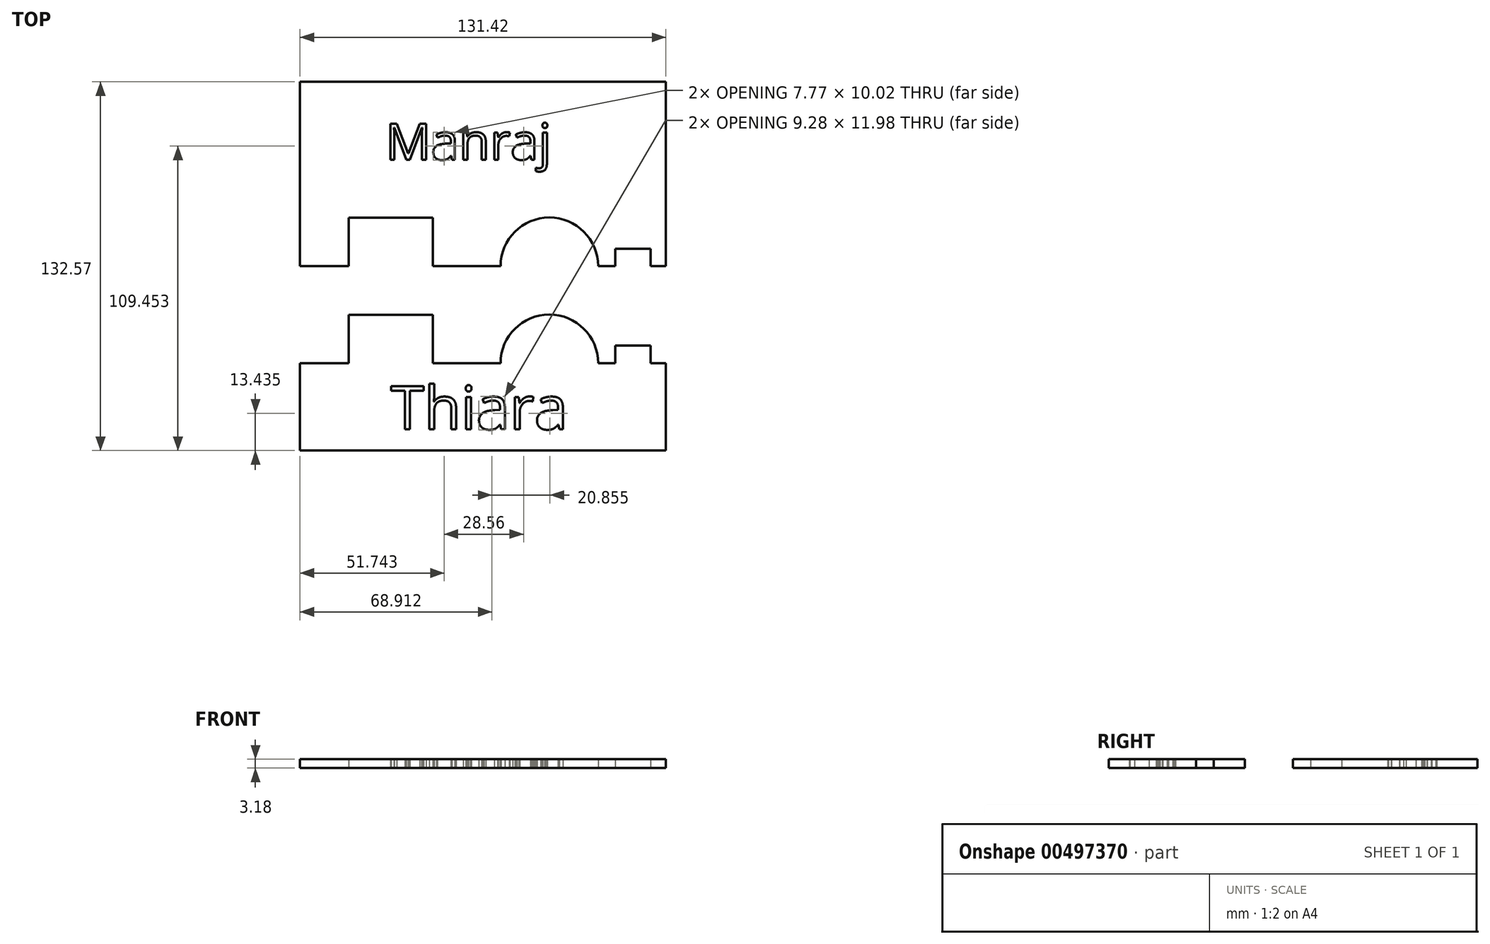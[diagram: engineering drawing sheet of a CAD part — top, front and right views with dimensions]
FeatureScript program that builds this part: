
annotation { "Feature Type Name" : "Feature", "Feature Type Description" : "" }
export const myFeature = defineFeature(function(context is Context, id is Id, definition is map)
    precondition{}
    {
        {
            var Q0;
            Q0=qCreatedBy(makeId("Top.planeOp"),FACE);
            var sketch = newSketch(context, id + "F0", { "sketchPlane" : qUnion([Q0])});
            skLineSegment(sketch, "E0.bottom", {"start": v(-79.32, 79.1) * mm, "end": v(52.1, 79.1) * mm});
            skLineSegment(sketch, "E0.top", {"start": v(-79.32, -53.48) * mm, "end": v(52.1, -53.48) * mm});
            skLineSegment(sketch, "E0.left", {"start": v(-79.32, 79.1) * mm, "end": v(-79.32, 12.8) * mm});
            skLineSegment(sketch, "E0.right", {"start": v(52.1, 79.1) * mm, "end": v(52.1, 12.8) * mm});
            skLineSegment(sketch, "E1", {"start": v(-79.32, 12.8) * mm, "end": v(-61.87, 12.8) * mm});
            skLineSegment(sketch, "E2.top", {"start": v(-61.87, 30.25) * mm, "end": v(-31.63, 30.25) * mm});
            skLineSegment(sketch, "E2.left", {"start": v(-61.87, 12.8) * mm, "end": v(-61.87, 30.25) * mm});
            skLineSegment(sketch, "E2.right", {"start": v(-31.63, 12.8) * mm, "end": v(-31.63, 30.25) * mm});
            skLineSegment(sketch, "E3.trimOffspring", {"start": v(-31.63, 12.8) * mm, "end": v(-7.29, 12.8) * mm});
            skLineSegment(sketch, "E4.trimOffspring", {"start": v(-79.32, -22.1) * mm, "end": v(-79.32, -53.48) * mm});
            skLineSegment(sketch, "E5.top", {"start": v(-79.32, -22.1) * mm, "end": v(-61.87, -22.1) * mm});
            skLineSegment(sketch, "E5.left", {"start": v(-79.32, -53.48) * mm, "end": v(-79.32, -22.1) * mm});
            skLineSegment(sketch, "E5.right", {"start": v(52.1, -53.48) * mm, "end": v(52.1, -22.1) * mm});
            skLineSegment(sketch, "E6.trimOffspring", {"start": v(52.1, -22.1) * mm, "end": v(52.1, -53.48) * mm});
            skLineSegment(sketch, "E7", {"start": v(-61.87, -4.65) * mm, "end": v(-61.87, -22.1) * mm});
            skLineSegment(sketch, "E8", {"start": v(-31.63, -4.65) * mm, "end": v(-31.63, -22.1) * mm});
            skLineSegment(sketch, "E9", {"start": v(-61.87, -4.65) * mm, "end": v(-31.63, -4.65) * mm});
            skLineSegment(sketch, "E10.trimOffspring", {"start": v(-31.63, -22.1) * mm, "end": v(-7.29, -22.1) * mm});
            skLineSegment(sketch, "E11.left", {"start": v(52.1, 12.8) * mm, "end": v(52.1, 79.69) * mm});
            skArc(sketch, "E12", {"start": v(27.75, 12.8) * mm, "mid": v(10.23, 30.32) * mm, "end": v(-7.29, 12.8) * mm});
            skLineSegment(sketch, "E13.trimOffspring", {"start": v(27.75, 12.8) * mm, "end": v(33.88, 12.8) * mm});
            skArc(sketch, "E14", {"start": v(27.75, -22.1) * mm, "mid": v(10.23, -4.58) * mm, "end": v(-7.29, -22.1) * mm});
            skLineSegment(sketch, "E15.trimOffspring", {"start": v(27.75, -22.1) * mm, "end": v(33.88, -22.1) * mm});
            skText(sketch, "E16", { "text": "Manraj", "fontName": "OpenSans-Regular.ttf"});
            skLineSegment(sketch, "E17.bottom", {"start": v(33.88, 19.14) * mm, "end": v(46.58, 19.14) * mm});
            skLineSegment(sketch, "E17.left", {"start": v(33.88, 19.14) * mm, "end": v(33.88, 12.79) * mm});
            skLineSegment(sketch, "E17.right", {"start": v(46.58, 19.14) * mm, "end": v(46.58, 12.79) * mm});
            skLineSegment(sketch, "E18.trimOffspring", {"start": v(46.58, 12.8) * mm, "end": v(52.1, 12.8) * mm});
            skLineSegment(sketch, "E19", {"start": v(33.88, 12.8) * mm, "end": v(33.88, 12.79) * mm});
            skLineSegment(sketch, "E20", {"start": v(46.58, 12.8) * mm, "end": v(46.58, 12.79) * mm});
            skLineSegment(sketch, "E21", {"start": v(33.88, -15.75) * mm, "end": v(46.58, -15.75) * mm});
            skLineSegment(sketch, "E22.trimOffspring", {"start": v(33.88, -15.75) * mm, "end": v(33.88, -22.1) * mm});
            skLineSegment(sketch, "E23.trimOffspring", {"start": v(46.58, -15.75) * mm, "end": v(46.58, -22.1) * mm});
            skLineSegment(sketch, "E24.trimOffspring", {"start": v(46.58, -22.1) * mm, "end": v(52.1, -22.1) * mm});
            skText(sketch, "E25", { "text": "Thiara", "fontName": "OpenSans-Regular.ttf"});
            skPoint(sketch, "E26", {"position": v(-46.75, -4.65) * mm});
            const initialGuessF0  = {"E16": [-0.04863, 0.05114, 1, 0, 0.01303], "E25": [-0.04675, -0.04582, 1, 0, 0.01557]};
            skSetInitialGuess(sketch, initialGuessF0);
            skSolve(sketch);
        }
        {
            var Q0;
            Q0 = qSketchRegion(id + "F0", true);
            extrude(context, id + "F1", {"entities" : qUnion([Q0]), "depth" : 3.17 * mm});
        }
    });
